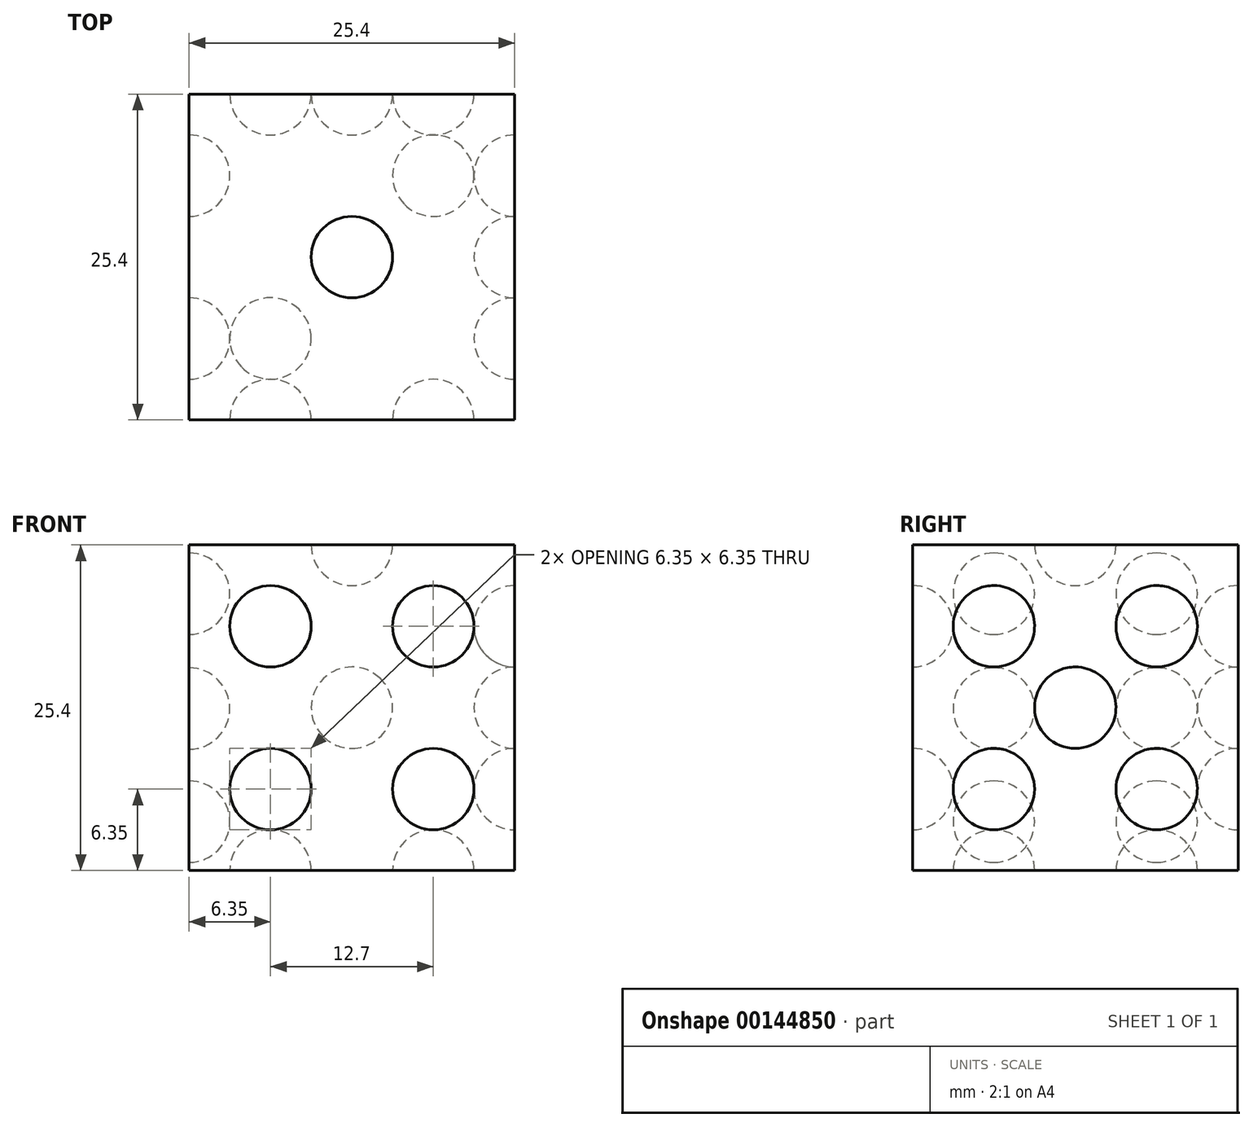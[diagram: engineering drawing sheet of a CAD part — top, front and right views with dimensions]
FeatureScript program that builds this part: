
annotation { "Feature Type Name" : "Feature", "Feature Type Description" : "" }
export const myFeature = defineFeature(function(context is Context, id is Id, definition is map)
    precondition{}
    {
        {
            var Q0;
            Q0=qCreatedBy(makeId("Top.planeOp"),FACE);
            var sketch = newSketch(context, id + "F0", { "sketchPlane" : qUnion([Q0])});
            skLineSegment(sketch, "E0.bottom", {"start": v(12.7, -12.7) * mm, "end": v(-12.7, -12.7) * mm});
            skLineSegment(sketch, "E0.top", {"start": v(12.7, 12.7) * mm, "end": v(-12.7, 12.7) * mm});
            skLineSegment(sketch, "E0.left", {"start": v(12.7, -12.7) * mm, "end": v(12.7, 12.7) * mm});
            skLineSegment(sketch, "E0.right", {"start": v(-12.7, -12.7) * mm, "end": v(-12.7, 12.7) * mm});
            skPoint(sketch, "E0.middle", {"position": v(0, 0) * mm});
            skSolve(sketch);
        }
        {
            var Q0;
            Q0=makeQuery(id+"F0.imprint","IMPRINT",FACE,{"disambiguationData":[TD([[makeQuery(id+"F0.imprint","IMPRINT",EDGE,{"derivedFrom":sQuery(id+"F0.wireOp",EDGE,"E0.bottom")}),-1.0]])]});
            extrude(context, id + "F1", {"entities" : qUnion([Q0]), "depth" : 25.4 * mm});
        }
        {
            var Q0;
            Q0=makeQuery(id+"F1.opExtrude","CAP_FACE",FACE,{"disambiguationData":[OSD([sQuery(id+"F0.wireOp",EDGE,"E0.bottom"),sQuery(id+"F0.wireOp",EDGE,"E0.top"),sQuery(id+"F0.wireOp",EDGE,"E0.left"),sQuery(id+"F0.wireOp",EDGE,"E0.right")])],"isStart":false});
            var sketch = newSketch(context, id + "F2", { "sketchPlane" : qUnion([Q0])});
            skArc(sketch, "E1", {"start": v(-3.18, 0) * mm, "mid": v(0, -3.18) * mm, "end": v(3.18, 0) * mm});
            skLineSegment(sketch, "E2", {"start": v(-5.07, 0) * mm, "end": v(4.76, 0) * mm});
            skSolve(sketch);
        }
        {
            var Q0;
            {var subQ0=sQuery(id+"F2.wireOp",EDGE,"E1");Q0=makeQuery(id+"F2.imprint","IMPRINT",FACE,{"disambiguationData":[TD([[makeQuery(id+"F2.imprint","IMPRINT",EDGE,{"derivedFrom":subQ0}),1.0]])]});}
            var Q1;
            Q1=sQuery(id+"F2.wireOp",EDGE,"E2");
            revolve(context, id + "F3", {"operationType" : NewBodyOperationType.REMOVE, "entities" : qUnion([Q0]), "axis" : qUnion([Q1]), "revolveType" : RevolveType.FULL, "oppositeDirection" : true});
        }
        {
            var Q0;
            Q0=makeQuery(id+"F1.opExtrude","CAP_FACE",FACE,{"disambiguationData":[OSD([sQuery(id+"F0.wireOp",EDGE,"E0.bottom"),sQuery(id+"F0.wireOp",EDGE,"E0.top"),sQuery(id+"F0.wireOp",EDGE,"E0.left"),sQuery(id+"F0.wireOp",EDGE,"E0.right")])],"isStart":true});
            var sketch = newSketch(context, id + "F4", { "sketchPlane" : qUnion([Q0])});
            skArc(sketch, "E3", {"start": v(-8.6, 8.6) * mm, "mid": v(-8.6, 4.1) * mm, "end": v(-4.1, 4.1) * mm});
            skArc(sketch, "E4", {"start": v(4.1, -4.1) * mm, "mid": v(4.1, -8.6) * mm, "end": v(8.6, -8.6) * mm});
            skLineSegment(sketch, "E5", {"start": v(-8.6, 8.6) * mm, "end": v(-4.1, 4.1) * mm});
            skLineSegment(sketch, "E6.trimOffspring", {"start": v(4.1, -4.1) * mm, "end": v(8.6, -8.6) * mm});
            skSolve(sketch);
        }
        {
            var Q0;
            Q0=makeQuery(id+"F4.imprint","IMPRINT",FACE,{"disambiguationData":[TD([[makeQuery(id+"F4.imprint","IMPRINT",EDGE,{"derivedFrom":sQuery(id+"F4.wireOp",EDGE,"E3")}),1.0]])]});
            var Q1;
            Q1=makeQuery(id+"F4.imprint","IMPRINT",FACE,{"disambiguationData":[TD([[makeQuery(id+"F4.imprint","IMPRINT",EDGE,{"derivedFrom":sQuery(id+"F4.wireOp",EDGE,"E4")}),1.0]])]});
            var Q2;
            Q2=sQuery(id+"F4.wireOp",EDGE,"E6.trimOffspring");
            revolve(context, id + "F5", {"operationType" : NewBodyOperationType.REMOVE, "entities" : qUnion([Q0, Q1]), "axis" : qUnion([Q2]), "revolveType" : RevolveType.FULL, "oppositeDirection" : true});
        }
        {
            var Q0;
            Q0=makeQuery(id+"F1.opExtrude","SWEPT_FACE",FACE,{"disambiguationData":[OSD([sQuery(id+"F0.wireOp",EDGE,"E0.top")])]});
            var sketch = newSketch(context, id + "F6", { "sketchPlane" : qUnion([Q0])});
            skArc(sketch, "E7", {"start": v(-8.6, 21.3) * mm, "mid": v(-8.6, 16.8) * mm, "end": v(-4.1, 16.8) * mm});
            skArc(sketch, "E8", {"start": v(4.1, 8.6) * mm, "mid": v(4.1, 4.1) * mm, "end": v(8.6, 4.1) * mm});
            skArc(sketch, "E9", {"start": v(-2.25, 14.95) * mm, "mid": v(-2.25, 10.45) * mm, "end": v(2.25, 10.45) * mm});
            skLineSegment(sketch, "E10", {"start": v(-12.7, 25.4) * mm, "end": v(12.7, 0) * mm});
            skSolve(sketch);
        }
        {
            var Q0;
            {var subQ0=sQuery(id+"F6.wireOp",EDGE,"E7");Q0=makeQuery(id+"F6.imprint","IMPRINT",FACE,{"disambiguationData":[TD([[makeQuery(id+"F6.imprint","IMPRINT",EDGE,{"derivedFrom":subQ0}),1.0]])]});}
            var Q1;
            {var subQ0=sQuery(id+"F6.wireOp",EDGE,"E9");Q1=makeQuery(id+"F6.imprint","IMPRINT",FACE,{"disambiguationData":[TD([[makeQuery(id+"F6.imprint","IMPRINT",EDGE,{"derivedFrom":subQ0}),1.0]])]});}
            var Q2;
            {var subQ0=sQuery(id+"F6.wireOp",EDGE,"E8");Q2=makeQuery(id+"F6.imprint","IMPRINT",FACE,{"disambiguationData":[TD([[makeQuery(id+"F6.imprint","IMPRINT",EDGE,{"derivedFrom":subQ0}),1.0]])]});}
            var Q3;
            Q3=sQuery(id+"F6.wireOp",EDGE,"E10");
            revolve(context, id + "F7", {"operationType" : NewBodyOperationType.REMOVE, "entities" : qUnion([Q0, Q1, Q2]), "axis" : qUnion([Q3]), "revolveType" : RevolveType.FULL, "oppositeDirection" : true});
        }
        {
            var Q0;
            Q0=makeQuery(id+"F1.opExtrude","SWEPT_FACE",FACE,{"disambiguationData":[OSD([sQuery(id+"F0.wireOp",EDGE,"E0.bottom")])]});
            var sketch = newSketch(context, id + "F8", { "sketchPlane" : qUnion([Q0])});
            skArc(sketch, "E11", {"start": v(-3.18, 19.05) * mm, "mid": v(-6.35, 22.23) * mm, "end": v(-9.53, 19.05) * mm});
            skArc(sketch, "E12", {"start": v(9.53, 19.05) * mm, "mid": v(6.35, 22.23) * mm, "end": v(3.18, 19.05) * mm});
            skArc(sketch, "E13", {"start": v(3.18, 6.35) * mm, "mid": v(6.35, 3.18) * mm, "end": v(9.53, 6.35) * mm});
            skArc(sketch, "E14", {"start": v(-9.53, 6.35) * mm, "mid": v(-6.35, 3.17) * mm, "end": v(-3.18, 6.35) * mm});
            skLineSegment(sketch, "E15", {"start": v(12.7, 19.05) * mm, "end": v(-12.7, 19.05) * mm});
            skLineSegment(sketch, "E16", {"start": v(-12.7, 6.35) * mm, "end": v(12.7, 6.35) * mm});
            skSolve(sketch);
        }
        {
            var Q0;
            {var subQ0=sQuery(id+"F8.wireOp",EDGE,"E13");Q0=makeQuery(id+"F8.imprint","IMPRINT",FACE,{"disambiguationData":[TD([[makeQuery(id+"F8.imprint","IMPRINT",EDGE,{"derivedFrom":subQ0}),1.0]])]});}
            var Q1;
            {var subQ0=sQuery(id+"F8.wireOp",EDGE,"E14");Q1=makeQuery(id+"F8.imprint","IMPRINT",FACE,{"disambiguationData":[TD([[makeQuery(id+"F8.imprint","IMPRINT",EDGE,{"derivedFrom":subQ0}),1.0]])]});}
            var Q2;
            Q2=sQuery(id+"F8.wireOp",EDGE,"E16");
            revolve(context, id + "F9", {"operationType" : NewBodyOperationType.REMOVE, "entities" : qUnion([Q0, Q1]), "axis" : qUnion([Q2]), "revolveType" : RevolveType.FULL, "oppositeDirection" : true});
        }
        {
            var Q0;
            {var subQ0=sQuery(id+"F8.wireOp",EDGE,"E11");Q0=makeQuery(id+"F8.imprint","IMPRINT",FACE,{"disambiguationData":[TD([[makeQuery(id+"F8.imprint","IMPRINT",EDGE,{"derivedFrom":subQ0}),1.0]])]});}
            var Q1;
            {var subQ0=sQuery(id+"F8.wireOp",EDGE,"E12");Q1=makeQuery(id+"F8.imprint","IMPRINT",FACE,{"disambiguationData":[TD([[makeQuery(id+"F8.imprint","IMPRINT",EDGE,{"derivedFrom":subQ0}),1.0]])]});}
            var Q2;
            Q2=sQuery(id+"F8.wireOp",EDGE,"E15");
            revolve(context, id + "F10", {"operationType" : NewBodyOperationType.REMOVE, "entities" : qUnion([Q0, Q1]), "axis" : qUnion([Q2]), "revolveType" : RevolveType.FULL, "oppositeDirection" : true});
        }
        {
            var Q0;
            Q0=makeQuery(id+"F1.opExtrude","SWEPT_FACE",FACE,{"disambiguationData":[OSD([sQuery(id+"F0.wireOp",EDGE,"E0.left")])]});
            var sketch = newSketch(context, id + "F11", { "sketchPlane" : qUnion([Q0])});
            skArc(sketch, "E17", {"start": v(-2.25, 14.95) * mm, "mid": v(-2.25, 10.45) * mm, "end": v(2.25, 10.45) * mm});
            skArc(sketch, "E18", {"start": v(-8.6, 21.3) * mm, "mid": v(-8.6, 16.8) * mm, "end": v(-4.1, 16.8) * mm});
            skArc(sketch, "E19", {"start": v(4.1, 16.8) * mm, "mid": v(8.6, 16.8) * mm, "end": v(8.6, 21.3) * mm});
            skArc(sketch, "E20", {"start": v(-8.6, 4.1) * mm, "mid": v(-4.1, 4.1) * mm, "end": v(-4.1, 8.6) * mm});
            skArc(sketch, "E21", {"start": v(4.1, 8.6) * mm, "mid": v(4.1, 4.1) * mm, "end": v(8.6, 4.1) * mm});
            skLineSegment(sketch, "E22", {"start": v(-8.6, 21.3) * mm, "end": v(-4.1, 16.8) * mm});
            skLineSegment(sketch, "E23", {"start": v(8.6, 21.3) * mm, "end": v(4.1, 16.8) * mm});
            skLineSegment(sketch, "E24.trimOffspring", {"start": v(-2.25, 14.95) * mm, "end": v(2.25, 10.45) * mm});
            skLineSegment(sketch, "E25.trimOffspring", {"start": v(-4.1, 8.6) * mm, "end": v(-8.6, 4.1) * mm});
            skLineSegment(sketch, "E26.trimOffspring", {"start": v(4.1, 8.6) * mm, "end": v(8.6, 4.1) * mm});
            skSolve(sketch);
        }
        {
            var Q0;
            Q0=makeQuery(id+"F11.imprint","IMPRINT",FACE,{"disambiguationData":[TD([[makeQuery(id+"F11.imprint","IMPRINT",EDGE,{"derivedFrom":sQuery(id+"F11.wireOp",EDGE,"E18")}),1.0]])]});
            var Q1;
            Q1=makeQuery(id+"F11.imprint","IMPRINT",FACE,{"disambiguationData":[TD([[makeQuery(id+"F11.imprint","IMPRINT",EDGE,{"derivedFrom":sQuery(id+"F11.wireOp",EDGE,"E17")}),1.0]])]});
            var Q2;
            Q2=makeQuery(id+"F11.imprint","IMPRINT",FACE,{"disambiguationData":[TD([[makeQuery(id+"F11.imprint","IMPRINT",EDGE,{"derivedFrom":sQuery(id+"F11.wireOp",EDGE,"E21")}),1.0]])]});
            var Q3;
            Q3=sQuery(id+"F11.wireOp",EDGE,"E24.trimOffspring");
            revolve(context, id + "F12", {"operationType" : NewBodyOperationType.REMOVE, "entities" : qUnion([Q0, Q1, Q2]), "axis" : qUnion([Q3]), "revolveType" : RevolveType.FULL, "oppositeDirection" : true});
        }
        {
            var Q0;
            Q0=makeQuery(id+"F11.imprint","IMPRINT",FACE,{"disambiguationData":[TD([[makeQuery(id+"F11.imprint","IMPRINT",EDGE,{"derivedFrom":sQuery(id+"F11.wireOp",EDGE,"E20")}),1.0]])]});
            var Q1;
            Q1=makeQuery(id+"F11.imprint","IMPRINT",FACE,{"disambiguationData":[TD([[makeQuery(id+"F11.imprint","IMPRINT",EDGE,{"derivedFrom":sQuery(id+"F11.wireOp",EDGE,"E19")}),1.0]])]});
            var Q2;
            Q2=sQuery(id+"F11.wireOp",EDGE,"E23");
            revolve(context, id + "F13", {"operationType" : NewBodyOperationType.REMOVE, "entities" : qUnion([Q0, Q1]), "axis" : qUnion([Q2]), "revolveType" : RevolveType.FULL, "oppositeDirection" : true});
        }
        {
            var Q0;
            Q0=makeQuery(id+"F1.opExtrude","SWEPT_FACE",FACE,{"disambiguationData":[OSD([sQuery(id+"F0.wireOp",EDGE,"E0.right")])]});
            var sketch = newSketch(context, id + "F14", { "sketchPlane" : qUnion([Q0])});
            skArc(sketch, "E27", {"start": v(6.35, 0.63) * mm, "mid": v(9.52, 3.8) * mm, "end": v(6.35, 6.99) * mm});
            skArc(sketch, "E28", {"start": v(-6.35, 6.99) * mm, "mid": v(-9.53, 3.81) * mm, "end": v(-6.35, 0.64) * mm});
            skArc(sketch, "E29", {"start": v(-6.35, 24.77) * mm, "mid": v(-9.53, 21.59) * mm, "end": v(-6.35, 18.41) * mm});
            skArc(sketch, "E30", {"start": v(6.35, 18.41) * mm, "mid": v(9.52, 21.59) * mm, "end": v(6.35, 24.77) * mm});
            skLineSegment(sketch, "E31", {"start": v(-12.7, 0) * mm, "end": v(-6.35, 0) * mm});
            skLineSegment(sketch, "E32", {"start": v(12.7, 0) * mm, "end": v(6.35, 0) * mm});
            skLineSegment(sketch, "E33", {"start": v(6.35, 0) * mm, "end": v(6.35, 30.29) * mm});
            skLineSegment(sketch, "E34", {"start": v(-6.35, 0) * mm, "end": v(-6.35, 30.74) * mm});
            skArc(sketch, "E35", {"start": v(6.35, 9.45) * mm, "mid": v(9.52, 12.63) * mm, "end": v(6.35, 15.8) * mm});
            skArc(sketch, "E36", {"start": v(-6.35, 15.8) * mm, "mid": v(-9.53, 12.63) * mm, "end": v(-6.35, 9.45) * mm});
            skSolve(sketch);
        }
        {
            var Q0;
            {var subQ0=sQuery(id+"F14.wireOp",EDGE,"E27");Q0=makeQuery(id+"F14.imprint","IMPRINT",FACE,{"disambiguationData":[TD([[makeQuery(id+"F14.imprint","IMPRINT",EDGE,{"derivedFrom":subQ0}),1.0]])]});}
            var Q1;
            {var subQ0=sQuery(id+"F14.wireOp",EDGE,"E35");Q1=makeQuery(id+"F14.imprint","IMPRINT",FACE,{"disambiguationData":[TD([[makeQuery(id+"F14.imprint","IMPRINT",EDGE,{"derivedFrom":subQ0}),1.0]])]});}
            var Q2;
            {var subQ0=sQuery(id+"F14.wireOp",EDGE,"E30");Q2=makeQuery(id+"F14.imprint","IMPRINT",FACE,{"disambiguationData":[TD([[makeQuery(id+"F14.imprint","IMPRINT",EDGE,{"derivedFrom":subQ0}),1.0]])]});}
            var Q3;
            Q3=sQuery(id+"F14.wireOp",EDGE,"E33");
            revolve(context, id + "F15", {"operationType" : NewBodyOperationType.REMOVE, "entities" : qUnion([Q0, Q1, Q2]), "axis" : qUnion([Q3]), "revolveType" : RevolveType.FULL, "oppositeDirection" : true});
        }
        {
            var Q0;
            {var subQ0=sQuery(id+"F14.wireOp",EDGE,"E28");Q0=makeQuery(id+"F14.imprint","IMPRINT",FACE,{"disambiguationData":[TD([[makeQuery(id+"F14.imprint","IMPRINT",EDGE,{"derivedFrom":subQ0}),1.0]])]});}
            var Q1;
            {var subQ0=sQuery(id+"F14.wireOp",EDGE,"E36");Q1=makeQuery(id+"F14.imprint","IMPRINT",FACE,{"disambiguationData":[TD([[makeQuery(id+"F14.imprint","IMPRINT",EDGE,{"derivedFrom":subQ0}),1.0]])]});}
            var Q2;
            {var subQ0=sQuery(id+"F14.wireOp",EDGE,"E29");Q2=makeQuery(id+"F14.imprint","IMPRINT",FACE,{"disambiguationData":[TD([[makeQuery(id+"F14.imprint","IMPRINT",EDGE,{"derivedFrom":subQ0}),1.0]])]});}
            var Q3;
            Q3=sQuery(id+"F14.wireOp",EDGE,"E34");
            revolve(context, id + "F16", {"operationType" : NewBodyOperationType.REMOVE, "entities" : qUnion([Q0, Q1, Q2]), "axis" : qUnion([Q3]), "revolveType" : RevolveType.FULL, "oppositeDirection" : true});
        }
    });
